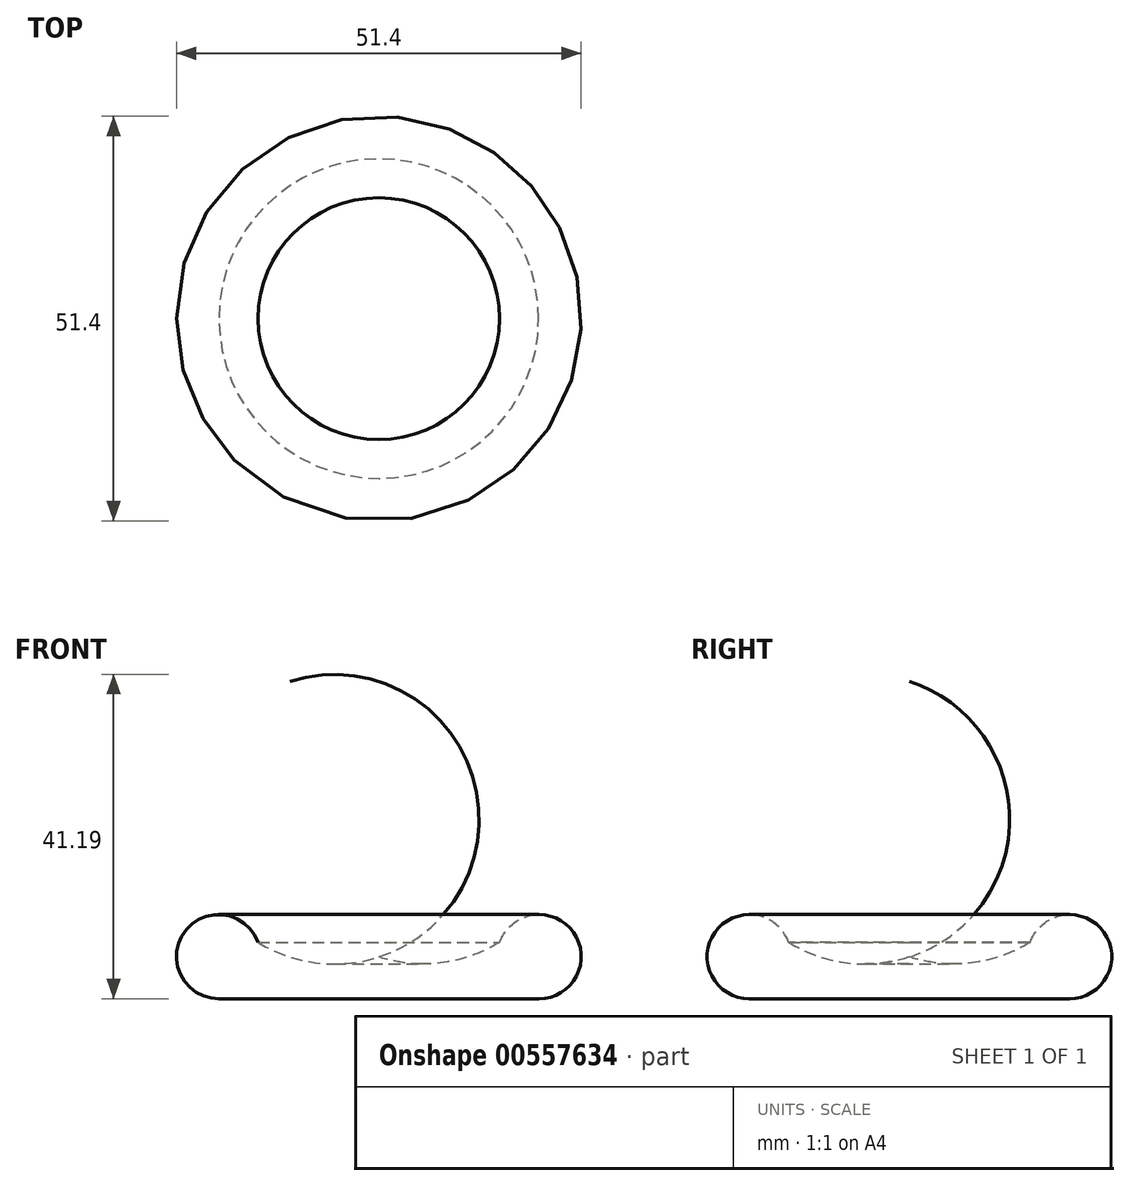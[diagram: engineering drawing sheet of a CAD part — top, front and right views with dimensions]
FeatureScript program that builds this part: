
annotation { "Feature Type Name" : "Feature", "Feature Type Description" : "" }
export const myFeature = defineFeature(function(context is Context, id is Id, definition is map)
    precondition{}
    {
        {
            var Q0;
            Q0=qCreatedBy(makeId("Front.planeOp"),FACE);
            var sketch = newSketch(context, id + "F0", { "sketchPlane" : qUnion([Q0])});
            skLineSegment(sketch, "E0.bottom", {"start": v(0, 0) * mm, "end": v(-20.3, 0) * mm});
            skLineSegment(sketch, "E0.left", {"start": v(0, 0) * mm, "end": v(0, 5.3) * mm});
            skArc(sketch, "E1", {"start": v(-15.35, 7.17) * mm, "mid": v(-7.88, 4.54) * mm, "end": v(0, 5.3) * mm});
            skCircle(sketch, "E2", {"center": v(-20.36, 5.34) * mm, "radius": 5.34 * mm});
            skPoint(sketch, "E2.third.point", {"position": v(-25.38, 7.17) * mm});
            skSolve(sketch);
        }
        {
            var Q0;
            Q0 = qSketchRegion(id + "F0", true);
            var Q1;
            Q1=sQuery(id+"F0.wireOp",EDGE,"E0.left");
            revolve(context, id + "F1", {"entities" : qUnion([Q0]), "axis" : qUnion([Q1]), "revolveType" : RevolveType.FULL});
        }
        {
            var Q0;
            Q0=qCreatedBy(makeId("Top.planeOp"),FACE);
            cPlane(context, id + "F2", {"entities" : qUnion([Q0]), "cplaneType" : CPlaneType.OFFSET, "offset" : 13 * mm, "width" : 152.4 * mm, "height" : 152.4 * mm});
        }
    });
